# Revit family: RN 55048 Optipress-Therm-Raccordo
name_source: partatom
category: Rohrformteile
units: mm (PartAtom-declared; Revit-internal decimal feet)

## family parameters
Arbeitsebenenbasiert = Nein
Beim Laden mit Abzugskörper schneiden = Nein
Bemaßung runder Anschluss = Durchmesser verwenden
Gemeinsam genutzt = Nein
Immer vertikal = Ja
Teiletyp = Verbindung

## types (17) — shared parameters
1.010.00.2 Blattnummer der Richtlinie = 29
1.010.00.3 Ausgabedatum (Monat) der Richtlinie = 201308
1.010.00.4 Herstellername = R. Nussbaum AG
1.010.00.5 Revisionsdatum der Datei = 20190521
1.010.00.6 Webadresse des Herstellers = http://www.nussbaum.ch
1.100.00.4 Produktbezeichnung = Versorgung
1.110.00.2 Index = 1
1.110.00.4 Produktbezeichnung = Optipress-Therm
1.960/3L.00.8 Link (URL) = https://www.nussbaum.ch
29.700.00.4 Produktname = Optipress-Therm-Anschlussverschraubung, mit Pressmuffe
29.700.00.5 Produktkennung = 2
29.700.00.6 Querschnittsform = 1
29.700.00.7 Nennweitensystem = DN
29.700.00.8 Nenndrucksystem = PN
29.710.02.4 Nenndruck = 16
29.710.02.5 max. zul. Überdruck [hPa] = 1600
29.710.02.7 max. zul. Dauer-Betriebsdruck [hPa] = 1600
29.710.02.9 max. zul. Dauer-Betriebstemperatur [°C] = 95
Connector Visibility = Nein
EnclosingSpace Visibility = Nein
R. Nussbaum AG 55048.25 de Visibility = Nein

## per-type parameters (varying)
- DN=12x15: 1.800.00.3 TGA-Nummer=01900100000000000000000000000000000000000000000027000000000000000018; 1.800.00.4 Kommentarfeld=55048.22, Optipress-Therm-Anschlussverschraubung, mit Pressmuffe, DN=12x15, L=37; 1.810.00.3 Hersteller-Bestellnummer=55048.22; 1.810.00.4 DATANORM-Nummer=55048.22; 1.810.00.6 GTIN-Nummer=7612945815002; 29.710.02.10 Formstück-Gewicht [kg]=0.046; 29.710.02.3 Benennung=Optipress-Therm-Anschlussverschraubung, mit Pressmuffe, DN=12x15, L=37; CONNECTOR0_DIAMETER_dX_0r=12 mm  [stored 0.0393701 ft]; CONNECTOR0_dX_01=22 mm; CONNECTOR0_ref_dX=22 mm; CONNECTOR1_DIAMETER_dX_0r=15 mm  [stored 0.0492126 ft]; CONNECTOR1_dX_00=31 mm  [stored 0.101706 ft]; CONNECTOR1_dX_01=44 mm; CONNECTOR1_ref_dX=31 mm  [stored 0.101706 ft]; R. Nussbaum AG 55048.22 de Visibility=Ja; R. Nussbaum AG 55048.23 de Visibility=Nein; R. Nussbaum AG 55048.24 de Visibility=Nein; R. Nussbaum AG 55048.26 de Visibility=Nein; R. Nussbaum AG 55048.27 de Visibility=Nein; R. Nussbaum AG 55048.28 de Visibility=Nein; R. Nussbaum AG 55048.29 de Visibility=Nein; R. Nussbaum AG 55048.30 de Visibility=Nein; R. Nussbaum AG 55048.31 de Visibility=Nein; R. Nussbaum AG 55048.32 de Visibility=Nein; R. Nussbaum AG 55048.33 de Visibility=Nein; R. Nussbaum AG 55048.34 de Visibility=Nein; R. Nussbaum AG 55048.35 de Visibility=Nein; R. Nussbaum AG 55048.36 de Visibility=Nein; R. Nussbaum AG 55048.37 de Visibility=Nein; R. Nussbaum AG 55048.38 de Visibility=Nein; R. Nussbaum AG 55048.40 de Visibility=Nein
- DN=15: 1.800.00.3 TGA-Nummer=01900100000000000000000000000000000000000000000027000000000000000017; 1.800.00.4 Kommentarfeld=55048.40, Optipress-Therm-Anschlussverschraubung, mit Pressmuffe, DN=15, L=36; 1.810.00.3 Hersteller-Bestellnummer=55048.4; 1.810.00.4 DATANORM-Nummer=55048.40; 1.810.00.5 StLB-Nummer=256.112; 1.810.00.6 GTIN-Nummer=7612945709011; 29.710.02.10 Formstück-Gewicht [kg]=0.063; 29.710.02.3 Benennung=Optipress-Therm-Anschlussverschraubung, mit Pressmuffe, DN=15, L=36; CONNECTOR0_DIAMETER_dX_0r=15 mm  [stored 0.0492126 ft]; CONNECTOR0_dX_01=22 mm; CONNECTOR0_ref_dX=22 mm; CONNECTOR1_DIAMETER_dX_0r=20 mm; CONNECTOR1_dX_00=29 mm; CONNECTOR1_dX_01=44 mm; CONNECTOR1_ref_dX=29 mm; Hersteller=R. Nussbaum AG; Modell=55048.4; R. Nussbaum AG 55048.22 de Visibility=Nein; R. Nussbaum AG 55048.23 de Visibility=Nein; R. Nussbaum AG 55048.24 de Visibility=Nein; R. Nussbaum AG 55048.26 de Visibility=Nein; R. Nussbaum AG 55048.27 de Visibility=Nein; R. Nussbaum AG 55048.28 de Visibility=Nein; R. Nussbaum AG 55048.29 de Visibility=Nein; R. Nussbaum AG 55048.30 de Visibility=Nein; R. Nussbaum AG 55048.31 de Visibility=Nein; R. Nussbaum AG 55048.32 de Visibility=Nein; R. Nussbaum AG 55048.33 de Visibility=Nein; R. Nussbaum AG 55048.34 de Visibility=Nein; R. Nussbaum AG 55048.35 de Visibility=Nein; R. Nussbaum AG 55048.36 de Visibility=Nein; R. Nussbaum AG 55048.37 de Visibility=Nein; R. Nussbaum AG 55048.38 de Visibility=Nein; R. Nussbaum AG 55048.40 de Visibility=Ja; Typenkommentare=Optipress-Therm-Raccordo  DN=15
- DN=50: 1.800.00.3 TGA-Nummer=01900100000000000000000000000000000000000000000027000000000000000016; 1.800.00.4 Kommentarfeld=55048.30, Optipress-Therm-Anschlussverschraubung, mit Pressmuffe, DN=50, L=53; 1.810.00.3 Hersteller-Bestellnummer=55048.3; 1.810.00.4 DATANORM-Nummer=55048.30; 1.810.00.5 StLB-Nummer=256.168; 1.810.00.6 GTIN-Nummer=7612945663665; 29.710.02.10 Formstück-Gewicht [kg]=0.506; 29.710.02.3 Benennung=Optipress-Therm-Anschlussverschraubung, mit Pressmuffe, DN=50, L=53; CONNECTOR0_DIAMETER_dX_0r=50 mm; CONNECTOR0_dX_01=40 mm; CONNECTOR0_ref_dX=40 mm; CONNECTOR1_DIAMETER_dX_0r=50 mm; CONNECTOR1_dX_00=44 mm; CONNECTOR1_dX_01=68 mm; CONNECTOR1_ref_dX=44 mm; Hersteller=R. Nussbaum AG; Modell=55048.3; R. Nussbaum AG 55048.22 de Visibility=Nein; R. Nussbaum AG 55048.23 de Visibility=Nein; R. Nussbaum AG 55048.24 de Visibility=Nein; R. Nussbaum AG 55048.26 de Visibility=Nein; R. Nussbaum AG 55048.27 de Visibility=Nein; R. Nussbaum AG 55048.28 de Visibility=Nein; R. Nussbaum AG 55048.29 de Visibility=Nein; R. Nussbaum AG 55048.30 de Visibility=Ja; R. Nussbaum AG 55048.31 de Visibility=Nein; R. Nussbaum AG 55048.32 de Visibility=Nein; R. Nussbaum AG 55048.33 de Visibility=Nein; R. Nussbaum AG 55048.34 de Visibility=Nein; R. Nussbaum AG 55048.35 de Visibility=Nein; R. Nussbaum AG 55048.36 de Visibility=Nein; R. Nussbaum AG 55048.37 de Visibility=Nein; R. Nussbaum AG 55048.38 de Visibility=Nein; R. Nussbaum AG 55048.40 de Visibility=Nein; Typenkommentare=Optipress-Therm-Raccordo  DN=50
- DN=1: 1.800.00.3 TGA-Nummer=01900100000000000000000000000000000000000000000027000000000000000015; 1.800.00.4 Kommentarfeld=55048.38, Optipress-Therm-Anschlussverschraubung, mit Pressmuffe, DN=20, L=39; 1.810.00.3 Hersteller-Bestellnummer=55048.38; 1.810.00.4 DATANORM-Nummer=55048.38; 1.810.00.5 StLB-Nummer=256.124; 1.810.00.6 GTIN-Nummer=7612945692160; 29.710.02.10 Formstück-Gewicht [kg]=0.078; 29.710.02.3 Benennung=Optipress-Therm-Anschlussverschraubung, mit Pressmuffe, DN=20, L=39; CONNECTOR0_DIAMETER_dX_0r=20 mm; CONNECTOR0_dX_01=24 mm  [stored 0.0787402 ft]; CONNECTOR0_ref_dX=24 mm  [stored 0.0787402 ft]; CONNECTOR1_DIAMETER_dX_0r=20 mm; CONNECTOR1_dX_00=33 mm; CONNECTOR1_dX_01=48 mm; CONNECTOR1_ref_dX=33 mm; Hersteller=R. Nussbaum AG; Modell=55048.38; R. Nussbaum AG 55048.22 de Visibility=Nein; R. Nussbaum AG 55048.23 de Visibility=Nein; R. Nussbaum AG 55048.24 de Visibility=Nein; R. Nussbaum AG 55048.26 de Visibility=Nein; R. Nussbaum AG 55048.27 de Visibility=Nein; R. Nussbaum AG 55048.28 de Visibility=Nein; R. Nussbaum AG 55048.29 de Visibility=Nein; R. Nussbaum AG 55048.30 de Visibility=Nein; R. Nussbaum AG 55048.31 de Visibility=Nein; R. Nussbaum AG 55048.32 de Visibility=Nein; R. Nussbaum AG 55048.33 de Visibility=Nein; R. Nussbaum AG 55048.34 de Visibility=Nein; R. Nussbaum AG 55048.35 de Visibility=Nein; R. Nussbaum AG 55048.36 de Visibility=Nein; R. Nussbaum AG 55048.37 de Visibility=Nein; R. Nussbaum AG 55048.38 de Visibility=Ja; R. Nussbaum AG 55048.40 de Visibility=Nein; Typenkommentare=Optipress-Therm-Raccordo  DN=20
- DN=2: 1.800.00.3 TGA-Nummer=01900100000000000000000000000000000000000000000027000000000000000014; 1.800.00.4 Kommentarfeld=55048.37, Optipress-Therm-Anschlussverschraubung, mit Pressmuffe, DN=25, L=46; 1.810.00.3 Hersteller-Bestellnummer=55048.37; 1.810.00.4 DATANORM-Nummer=55048.37; 1.810.00.5 StLB-Nummer=256.135; 1.810.00.6 GTIN-Nummer=7612945688286; 29.710.02.10 Formstück-Gewicht [kg]=0.119; 29.710.02.3 Benennung=Optipress-Therm-Anschlussverschraubung, mit Pressmuffe, DN=25, L=46; CONNECTOR0_DIAMETER_dX_0r=25 mm  [stored 0.082021 ft]; CONNECTOR0_dX_01=24 mm  [stored 0.0787402 ft]; CONNECTOR0_ref_dX=24 mm  [stored 0.0787402 ft]; CONNECTOR1_DIAMETER_dX_0r=25 mm  [stored 0.082021 ft]; CONNECTOR1_dX_00=40 mm; CONNECTOR1_dX_01=57 mm; CONNECTOR1_ref_dX=40 mm; Hersteller=R. Nussbaum AG; Modell=55048.37; R. Nussbaum AG 55048.22 de Visibility=Nein; R. Nussbaum AG 55048.23 de Visibility=Nein; R. Nussbaum AG 55048.24 de Visibility=Nein; R. Nussbaum AG 55048.26 de Visibility=Nein; R. Nussbaum AG 55048.27 de Visibility=Nein; R. Nussbaum AG 55048.28 de Visibility=Nein; R. Nussbaum AG 55048.29 de Visibility=Nein; R. Nussbaum AG 55048.30 de Visibility=Nein; R. Nussbaum AG 55048.31 de Visibility=Nein; R. Nussbaum AG 55048.32 de Visibility=Nein; R. Nussbaum AG 55048.33 de Visibility=Nein; R. Nussbaum AG 55048.34 de Visibility=Nein; R. Nussbaum AG 55048.35 de Visibility=Nein; R. Nussbaum AG 55048.36 de Visibility=Nein; R. Nussbaum AG 55048.37 de Visibility=Ja; R. Nussbaum AG 55048.38 de Visibility=Nein; R. Nussbaum AG 55048.40 de Visibility=Nein; Typenkommentare=Optipress-Therm-Raccordo  DN=25
- DN=50x65: 1.800.00.3 TGA-Nummer=01900100000000000000000000000000000000000000000027000000000000000013; 1.800.00.4 Kommentarfeld=55048.36, Optipress-Therm-Anschlussverschraubung, mit Pressmuffe, DN=50x65, L=55; 1.810.00.3 Hersteller-Bestellnummer=55048.36; 1.810.00.4 DATANORM-Nummer=55048.36; 1.810.00.5 StLB-Nummer=256.168; 1.810.00.6 GTIN-Nummer=7612945685940; 29.710.02.10 Formstück-Gewicht [kg]=0.642; 29.710.02.3 Benennung=Optipress-Therm-Anschlussverschraubung, mit Pressmuffe, DN=50x65, L=55; CONNECTOR0_DIAMETER_dX_0r=50 mm; CONNECTOR0_dX_01=40 mm; CONNECTOR0_ref_dX=40 mm; CONNECTOR1_DIAMETER_dX_0r=65 mm; CONNECTOR1_dX_00=45 mm  [stored 0.147638 ft]; CONNECTOR1_dX_01=72 mm; CONNECTOR1_ref_dX=45 mm  [stored 0.147638 ft]; Hersteller=R. Nussbaum AG; Modell=55048.36; R. Nussbaum AG 55048.22 de Visibility=Nein; R. Nussbaum AG 55048.23 de Visibility=Nein; R. Nussbaum AG 55048.24 de Visibility=Nein; R. Nussbaum AG 55048.26 de Visibility=Nein; R. Nussbaum AG 55048.27 de Visibility=Nein; R. Nussbaum AG 55048.28 de Visibility=Nein; R. Nussbaum AG 55048.29 de Visibility=Nein; R. Nussbaum AG 55048.30 de Visibility=Nein; R. Nussbaum AG 55048.31 de Visibility=Nein; R. Nussbaum AG 55048.32 de Visibility=Nein; R. Nussbaum AG 55048.33 de Visibility=Nein; R. Nussbaum AG 55048.34 de Visibility=Nein; R. Nussbaum AG 55048.35 de Visibility=Nein; R. Nussbaum AG 55048.36 de Visibility=Ja; R. Nussbaum AG 55048.37 de Visibility=Nein; R. Nussbaum AG 55048.38 de Visibility=Nein; R. Nussbaum AG 55048.40 de Visibility=Nein; Typenkommentare=Optipress-Therm-Raccordo  DN=50x65
- DN=40x50: 1.800.00.3 TGA-Nummer=01900100000000000000000000000000000000000000000027000000000000000012; 1.800.00.4 Kommentarfeld=55048.35, Optipress-Therm-Anschlussverschraubung, mit Pressmuffe, DN=40x50, L=54; 1.810.00.3 Hersteller-Bestellnummer=55048.35; 1.810.00.4 DATANORM-Nummer=55048.35; 1.810.00.5 StLB-Nummer=256.157; 1.810.00.6 GTIN-Nummer=7612945685933; 29.710.02.10 Formstück-Gewicht [kg]=0.344; 29.710.02.3 Benennung=Optipress-Therm-Anschlussverschraubung, mit Pressmuffe, DN=40x50, L=54; CONNECTOR0_DIAMETER_dX_0r=40 mm; CONNECTOR0_dX_01=36 mm; CONNECTOR0_ref_dX=36 mm; CONNECTOR1_DIAMETER_dX_0r=50 mm; CONNECTOR1_dX_00=46 mm; CONNECTOR1_dX_01=70 mm; CONNECTOR1_ref_dX=46 mm; Hersteller=R. Nussbaum AG; Modell=55048.35; R. Nussbaum AG 55048.22 de Visibility=Nein; R. Nussbaum AG 55048.23 de Visibility=Nein; R. Nussbaum AG 55048.24 de Visibility=Nein; R. Nussbaum AG 55048.26 de Visibility=Nein; R. Nussbaum AG 55048.27 de Visibility=Nein; R. Nussbaum AG 55048.28 de Visibility=Nein; R. Nussbaum AG 55048.29 de Visibility=Nein; R. Nussbaum AG 55048.30 de Visibility=Nein; R. Nussbaum AG 55048.31 de Visibility=Nein; R. Nussbaum AG 55048.32 de Visibility=Nein; R. Nussbaum AG 55048.33 de Visibility=Nein; R. Nussbaum AG 55048.34 de Visibility=Nein; R. Nussbaum AG 55048.35 de Visibility=Ja; R. Nussbaum AG 55048.36 de Visibility=Nein; R. Nussbaum AG 55048.37 de Visibility=Nein; R. Nussbaum AG 55048.38 de Visibility=Nein; R. Nussbaum AG 55048.40 de Visibility=Nein; Typenkommentare=Optipress-Therm-Raccordo  DN=40x50
- DN=32x50: 1.800.00.3 TGA-Nummer=01900100000000000000000000000000000000000000000027000000000000000011; 1.800.00.4 Kommentarfeld=55048.34, Optipress-Therm-Anschlussverschraubung, mit Pressmuffe, DN=32x50, L=38; 1.810.00.3 Hersteller-Bestellnummer=55048.34; 1.810.00.4 DATANORM-Nummer=55048.34; 1.810.00.5 StLB-Nummer=256.146; 1.810.00.6 GTIN-Nummer=7612945685926; 29.710.02.10 Formstück-Gewicht [kg]=0.26; 29.710.02.3 Benennung=Optipress-Therm-Anschlussverschraubung, mit Pressmuffe, DN=32x50, L=38; CONNECTOR0_DIAMETER_dX_0r=32 mm  [stored 0.104987 ft]; CONNECTOR0_dX_01=26 mm; CONNECTOR0_ref_dX=26 mm; CONNECTOR1_DIAMETER_dX_0r=50 mm; CONNECTOR1_dX_00=27 mm; CONNECTOR1_dX_01=51 mm; CONNECTOR1_ref_dX=27 mm; Hersteller=R. Nussbaum AG; Modell=55048.34; R. Nussbaum AG 55048.22 de Visibility=Nein; R. Nussbaum AG 55048.23 de Visibility=Nein; R. Nussbaum AG 55048.24 de Visibility=Nein; R. Nussbaum AG 55048.26 de Visibility=Nein; R. Nussbaum AG 55048.27 de Visibility=Nein; R. Nussbaum AG 55048.28 de Visibility=Nein; R. Nussbaum AG 55048.29 de Visibility=Nein; R. Nussbaum AG 55048.30 de Visibility=Nein; R. Nussbaum AG 55048.31 de Visibility=Nein; R. Nussbaum AG 55048.32 de Visibility=Nein; R. Nussbaum AG 55048.33 de Visibility=Nein; R. Nussbaum AG 55048.34 de Visibility=Ja; R. Nussbaum AG 55048.35 de Visibility=Nein; R. Nussbaum AG 55048.36 de Visibility=Nein; R. Nussbaum AG 55048.37 de Visibility=Nein; R. Nussbaum AG 55048.38 de Visibility=Nein; R. Nussbaum AG 55048.40 de Visibility=Nein; Typenkommentare=Optipress-Therm-Raccordo  DN=32x50
- DN=25x32: 1.800.00.3 TGA-Nummer=01900100000000000000000000000000000000000000000027000000000000000010; 1.800.00.4 Kommentarfeld=55048.33, Optipress-Therm-Anschlussverschraubung, mit Pressmuffe, DN=25x32, L=36; 1.810.00.3 Hersteller-Bestellnummer=55048.33; 1.810.00.4 DATANORM-Nummer=55048.33; 1.810.00.5 StLB-Nummer=256.135; 1.810.00.6 GTIN-Nummer=7612945685919; 29.710.02.10 Formstück-Gewicht [kg]=0.174; 29.710.02.3 Benennung=Optipress-Therm-Anschlussverschraubung, mit Pressmuffe, DN=25x32, L=36; CONNECTOR0_DIAMETER_dX_0r=25 mm  [stored 0.082021 ft]; CONNECTOR0_dX_01=24 mm  [stored 0.0787402 ft]; CONNECTOR0_ref_dX=24 mm  [stored 0.0787402 ft]; CONNECTOR1_DIAMETER_dX_0r=40 mm; CONNECTOR1_dX_00=31 mm  [stored 0.101706 ft]; CONNECTOR1_dX_01=50 mm; CONNECTOR1_ref_dX=31 mm  [stored 0.101706 ft]; Hersteller=R. Nussbaum AG; Modell=55048.33; R. Nussbaum AG 55048.22 de Visibility=Nein; R. Nussbaum AG 55048.23 de Visibility=Nein; R. Nussbaum AG 55048.24 de Visibility=Nein; R. Nussbaum AG 55048.26 de Visibility=Nein; R. Nussbaum AG 55048.27 de Visibility=Nein; R. Nussbaum AG 55048.28 de Visibility=Nein; R. Nussbaum AG 55048.29 de Visibility=Nein; R. Nussbaum AG 55048.30 de Visibility=Nein; R. Nussbaum AG 55048.31 de Visibility=Nein; R. Nussbaum AG 55048.32 de Visibility=Nein; R. Nussbaum AG 55048.33 de Visibility=Ja; R. Nussbaum AG 55048.34 de Visibility=Nein; R. Nussbaum AG 55048.35 de Visibility=Nein; R. Nussbaum AG 55048.36 de Visibility=Nein; R. Nussbaum AG 55048.37 de Visibility=Nein; R. Nussbaum AG 55048.38 de Visibility=Nein; R. Nussbaum AG 55048.40 de Visibility=Nein; Typenkommentare=Optipress-Therm-Raccordo  DN=25x32
- DN=20x32: 1.800.00.3 TGA-Nummer=01900100000000000000000000000000000000000000000027000000000000000009; 1.800.00.4 Kommentarfeld=55048.32, Optipress-Therm-Anschlussverschraubung, mit Pressmuffe, DN=20x32, L=35; 1.810.00.3 Hersteller-Bestellnummer=55048.32; 1.810.00.4 DATANORM-Nummer=55048.32; 1.810.00.5 StLB-Nummer=256.124; 1.810.00.6 GTIN-Nummer=7612945685902; 29.710.02.10 Formstück-Gewicht [kg]=0.168; 29.710.02.3 Benennung=Optipress-Therm-Anschlussverschraubung, mit Pressmuffe, DN=20x32, L=35; CONNECTOR0_DIAMETER_dX_0r=20 mm; CONNECTOR0_dX_01=24 mm  [stored 0.0787402 ft]; CONNECTOR0_ref_dX=24 mm  [stored 0.0787402 ft]; CONNECTOR1_DIAMETER_dX_0r=40 mm; CONNECTOR1_dX_00=29 mm; CONNECTOR1_dX_01=48 mm; CONNECTOR1_ref_dX=29 mm; Hersteller=R. Nussbaum AG; Modell=55048.32; R. Nussbaum AG 55048.22 de Visibility=Nein; R. Nussbaum AG 55048.23 de Visibility=Nein; R. Nussbaum AG 55048.24 de Visibility=Nein; R. Nussbaum AG 55048.26 de Visibility=Nein; R. Nussbaum AG 55048.27 de Visibility=Nein; R. Nussbaum AG 55048.28 de Visibility=Nein; R. Nussbaum AG 55048.29 de Visibility=Nein; R. Nussbaum AG 55048.30 de Visibility=Nein; R. Nussbaum AG 55048.31 de Visibility=Nein; R. Nussbaum AG 55048.32 de Visibility=Ja; R. Nussbaum AG 55048.33 de Visibility=Nein; R. Nussbaum AG 55048.34 de Visibility=Nein; R. Nussbaum AG 55048.35 de Visibility=Nein; R. Nussbaum AG 55048.36 de Visibility=Nein; R. Nussbaum AG 55048.37 de Visibility=Nein; R. Nussbaum AG 55048.38 de Visibility=Nein; R. Nussbaum AG 55048.40 de Visibility=Nein; Typenkommentare=Optipress-Therm-Raccordo  DN=20x32
- DN=20x25: 1.800.00.3 TGA-Nummer=01900100000000000000000000000000000000000000000027000000000000000008; 1.800.00.4 Kommentarfeld=55048.31, Optipress-Therm-Anschlussverschraubung, mit Pressmuffe, DN=20x25, L=34; 1.810.00.3 Hersteller-Bestellnummer=55048.31; 1.810.00.4 DATANORM-Nummer=55048.31; 1.810.00.5 StLB-Nummer=256.124; 1.810.00.6 GTIN-Nummer=7612945685896; 29.710.02.10 Formstück-Gewicht [kg]=0.183; 29.710.02.3 Benennung=Optipress-Therm-Anschlussverschraubung, mit Pressmuffe, DN=20x25, L=34; CONNECTOR0_DIAMETER_dX_0r=20 mm; CONNECTOR0_dX_01=24 mm  [stored 0.0787402 ft]; CONNECTOR0_ref_dX=24 mm  [stored 0.0787402 ft]; CONNECTOR1_DIAMETER_dX_0r=32 mm  [stored 0.104987 ft]; CONNECTOR1_dX_00=28 mm; CONNECTOR1_dX_01=47 mm; CONNECTOR1_ref_dX=28 mm; Hersteller=R. Nussbaum AG; Modell=55048.31; R. Nussbaum AG 55048.22 de Visibility=Nein; R. Nussbaum AG 55048.23 de Visibility=Nein; R. Nussbaum AG 55048.24 de Visibility=Nein; R. Nussbaum AG 55048.26 de Visibility=Nein; R. Nussbaum AG 55048.27 de Visibility=Nein; R. Nussbaum AG 55048.28 de Visibility=Nein; R. Nussbaum AG 55048.29 de Visibility=Nein; R. Nussbaum AG 55048.30 de Visibility=Nein; R. Nussbaum AG 55048.31 de Visibility=Ja; R. Nussbaum AG 55048.32 de Visibility=Nein; R. Nussbaum AG 55048.33 de Visibility=Nein; R. Nussbaum AG 55048.34 de Visibility=Nein; R. Nussbaum AG 55048.35 de Visibility=Nein; R. Nussbaum AG 55048.36 de Visibility=Nein; R. Nussbaum AG 55048.37 de Visibility=Nein; R. Nussbaum AG 55048.38 de Visibility=Nein; R. Nussbaum AG 55048.40 de Visibility=Nein; Typenkommentare=Optipress-Therm-Raccordo  DN=20x25
- DN=40: 1.800.00.3 TGA-Nummer=01900100000000000000000000000000000000000000000027000000000000000007; 1.800.00.4 Kommentarfeld=55048.29, Optipress-Therm-Anschlussverschraubung, mit Pressmuffe, DN=40, L=46; 1.810.00.3 Hersteller-Bestellnummer=55048.29; 1.810.00.4 DATANORM-Nummer=55048.29; 1.810.00.5 StLB-Nummer=256.157; 1.810.00.6 GTIN-Nummer=7612945663658; 29.710.02.10 Formstück-Gewicht [kg]=0.281; 29.710.02.3 Benennung=Optipress-Therm-Anschlussverschraubung, mit Pressmuffe, DN=40, L=46; CONNECTOR0_DIAMETER_dX_0r=40 mm; CONNECTOR0_dX_01=36 mm; CONNECTOR0_ref_dX=36 mm; CONNECTOR1_DIAMETER_dX_0r=40 mm; CONNECTOR1_dX_00=40 mm; CONNECTOR1_dX_01=59 mm; CONNECTOR1_ref_dX=40 mm; Hersteller=R. Nussbaum AG; Modell=55048.29; R. Nussbaum AG 55048.22 de Visibility=Nein; R. Nussbaum AG 55048.23 de Visibility=Nein; R. Nussbaum AG 55048.24 de Visibility=Nein; R. Nussbaum AG 55048.26 de Visibility=Nein; R. Nussbaum AG 55048.27 de Visibility=Nein; R. Nussbaum AG 55048.28 de Visibility=Nein; R. Nussbaum AG 55048.29 de Visibility=Ja; R. Nussbaum AG 55048.30 de Visibility=Nein; R. Nussbaum AG 55048.31 de Visibility=Nein; R. Nussbaum AG 55048.32 de Visibility=Nein; R. Nussbaum AG 55048.33 de Visibility=Nein; R. Nussbaum AG 55048.34 de Visibility=Nein; R. Nussbaum AG 55048.35 de Visibility=Nein; R. Nussbaum AG 55048.36 de Visibility=Nein; R. Nussbaum AG 55048.37 de Visibility=Nein; R. Nussbaum AG 55048.38 de Visibility=Nein; R. Nussbaum AG 55048.40 de Visibility=Nein; Typenkommentare=Optipress-Therm-Raccordo  DN=40
- DN=32: 1.800.00.3 TGA-Nummer=01900100000000000000000000000000000000000000000027000000000000000006; 1.800.00.4 Kommentarfeld=55048.28, Optipress-Therm-Anschlussverschraubung, mit Pressmuffe, DN=32, L=37; 1.810.00.3 Hersteller-Bestellnummer=55048.28; 1.810.00.4 DATANORM-Nummer=55048.28; 1.810.00.5 StLB-Nummer=256.146; 1.810.00.6 GTIN-Nummer=7612945663641; 29.710.02.10 Formstück-Gewicht [kg]=0.188; 29.710.02.3 Benennung=Optipress-Therm-Anschlussverschraubung, mit Pressmuffe, DN=32, L=37; CONNECTOR0_DIAMETER_dX_0r=32 mm  [stored 0.104987 ft]; CONNECTOR0_dX_01=26 mm; CONNECTOR0_ref_dX=26 mm; CONNECTOR1_DIAMETER_dX_0r=40 mm; CONNECTOR1_dX_00=30 mm  [stored 0.0984252 ft]; CONNECTOR1_dX_01=49 mm; CONNECTOR1_ref_dX=30 mm  [stored 0.0984252 ft]; R. Nussbaum AG 55048.22 de Visibility=Nein; R. Nussbaum AG 55048.23 de Visibility=Nein; R. Nussbaum AG 55048.24 de Visibility=Nein; R. Nussbaum AG 55048.26 de Visibility=Nein; R. Nussbaum AG 55048.27 de Visibility=Nein; R. Nussbaum AG 55048.28 de Visibility=Ja; R. Nussbaum AG 55048.29 de Visibility=Nein; R. Nussbaum AG 55048.30 de Visibility=Nein; R. Nussbaum AG 55048.31 de Visibility=Nein; R. Nussbaum AG 55048.32 de Visibility=Nein; R. Nussbaum AG 55048.33 de Visibility=Nein; R. Nussbaum AG 55048.34 de Visibility=Nein; R. Nussbaum AG 55048.35 de Visibility=Nein; R. Nussbaum AG 55048.36 de Visibility=Nein; R. Nussbaum AG 55048.37 de Visibility=Nein; R. Nussbaum AG 55048.38 de Visibility=Nein; R. Nussbaum AG 55048.40 de Visibility=Nein
- DN=25: 1.800.00.3 TGA-Nummer=01900100000000000000000000000000000000000000000027000000000000000005; 1.800.00.4 Kommentarfeld=55048.27, Optipress-Therm-Anschlussverschraubung, mit Pressmuffe, DN=25, L=38; 1.810.00.3 Hersteller-Bestellnummer=55048.27; 1.810.00.4 DATANORM-Nummer=55048.27; 1.810.00.5 StLB-Nummer=256.135; 1.810.00.6 GTIN-Nummer=7612945663634; 29.710.02.10 Formstück-Gewicht [kg]=0.149; 29.710.02.3 Benennung=Optipress-Therm-Anschlussverschraubung, mit Pressmuffe, DN=25, L=38; CONNECTOR0_DIAMETER_dX_0r=25 mm  [stored 0.082021 ft]; CONNECTOR0_dX_01=24 mm  [stored 0.0787402 ft]; CONNECTOR0_ref_dX=24 mm  [stored 0.0787402 ft]; CONNECTOR1_DIAMETER_dX_0r=32 mm  [stored 0.104987 ft]; CONNECTOR1_dX_00=29 mm; CONNECTOR1_dX_01=48 mm; CONNECTOR1_ref_dX=29 mm; R. Nussbaum AG 55048.22 de Visibility=Nein; R. Nussbaum AG 55048.23 de Visibility=Nein; R. Nussbaum AG 55048.24 de Visibility=Nein; R. Nussbaum AG 55048.26 de Visibility=Nein; R. Nussbaum AG 55048.27 de Visibility=Ja; R. Nussbaum AG 55048.28 de Visibility=Nein; R. Nussbaum AG 55048.29 de Visibility=Nein; R. Nussbaum AG 55048.30 de Visibility=Nein; R. Nussbaum AG 55048.31 de Visibility=Nein; R. Nussbaum AG 55048.32 de Visibility=Nein; R. Nussbaum AG 55048.33 de Visibility=Nein; R. Nussbaum AG 55048.34 de Visibility=Nein; R. Nussbaum AG 55048.35 de Visibility=Nein; R. Nussbaum AG 55048.36 de Visibility=Nein; R. Nussbaum AG 55048.37 de Visibility=Nein; R. Nussbaum AG 55048.38 de Visibility=Nein; R. Nussbaum AG 55048.40 de Visibility=Nein
- DN=20: 1.800.00.3 TGA-Nummer=01900100000000000000000000000000000000000000000027000000000000000004; 1.800.00.4 Kommentarfeld=55048.26, Optipress-Therm-Anschlussverschraubung, mit Pressmuffe, DN=20, L=35; 1.810.00.3 Hersteller-Bestellnummer=55048.26; 1.810.00.4 DATANORM-Nummer=55048.26; 1.810.00.5 StLB-Nummer=256.124; 1.810.00.6 GTIN-Nummer=7612945663627; 29.710.02.10 Formstück-Gewicht [kg]=0.094; 29.710.02.3 Benennung=Optipress-Therm-Anschlussverschraubung, mit Pressmuffe, DN=20, L=35; CONNECTOR0_DIAMETER_dX_0r=20 mm; CONNECTOR0_dX_01=24 mm  [stored 0.0787402 ft]; CONNECTOR0_ref_dX=24 mm  [stored 0.0787402 ft]; CONNECTOR1_DIAMETER_dX_0r=25 mm  [stored 0.082021 ft]; CONNECTOR1_dX_00=27 mm; CONNECTOR1_dX_01=44 mm; CONNECTOR1_ref_dX=27 mm; R. Nussbaum AG 55048.22 de Visibility=Nein; R. Nussbaum AG 55048.23 de Visibility=Nein; R. Nussbaum AG 55048.24 de Visibility=Nein; R. Nussbaum AG 55048.26 de Visibility=Ja; R. Nussbaum AG 55048.27 de Visibility=Nein; R. Nussbaum AG 55048.28 de Visibility=Nein; R. Nussbaum AG 55048.29 de Visibility=Nein; R. Nussbaum AG 55048.30 de Visibility=Nein; R. Nussbaum AG 55048.31 de Visibility=Nein; R. Nussbaum AG 55048.32 de Visibility=Nein; R. Nussbaum AG 55048.33 de Visibility=Nein; R. Nussbaum AG 55048.34 de Visibility=Nein; R. Nussbaum AG 55048.35 de Visibility=Nein; R. Nussbaum AG 55048.36 de Visibility=Nein; R. Nussbaum AG 55048.37 de Visibility=Nein; R. Nussbaum AG 55048.38 de Visibility=Nein; R. Nussbaum AG 55048.40 de Visibility=Nein
- DN=15x20: 1.800.00.3 TGA-Nummer=01900100000000000000000000000000000000000000000027000000000000000002; 1.800.00.4 Kommentarfeld=55048.24, Optipress-Therm-Anschlussverschraubung, mit Pressmuffe, DN=15x20, L=31; 1.810.00.3 Hersteller-Bestellnummer=55048.24; 1.810.00.4 DATANORM-Nummer=55048.24; 1.810.00.5 StLB-Nummer=256.112; 1.810.00.6 GTIN-Nummer=7612945685872; 29.710.02.10 Formstück-Gewicht [kg]=0.076; 29.710.02.3 Benennung=Optipress-Therm-Anschlussverschraubung, mit Pressmuffe, DN=15x20, L=31; CONNECTOR0_DIAMETER_dX_0r=15 mm  [stored 0.0492126 ft]; CONNECTOR0_dX_01=22 mm; CONNECTOR0_ref_dX=22 mm; CONNECTOR1_DIAMETER_dX_0r=20 mm; CONNECTOR1_dX_00=24 mm  [stored 0.0787402 ft]; CONNECTOR1_dX_01=41 mm; CONNECTOR1_ref_dX=24 mm  [stored 0.0787402 ft]; R. Nussbaum AG 55048.22 de Visibility=Nein; R. Nussbaum AG 55048.23 de Visibility=Nein; R. Nussbaum AG 55048.24 de Visibility=Ja; R. Nussbaum AG 55048.26 de Visibility=Nein; R. Nussbaum AG 55048.27 de Visibility=Nein; R. Nussbaum AG 55048.28 de Visibility=Nein; R. Nussbaum AG 55048.29 de Visibility=Nein; R. Nussbaum AG 55048.30 de Visibility=Nein; R. Nussbaum AG 55048.31 de Visibility=Nein; R. Nussbaum AG 55048.32 de Visibility=Nein; R. Nussbaum AG 55048.33 de Visibility=Nein; R. Nussbaum AG 55048.34 de Visibility=Nein; R. Nussbaum AG 55048.35 de Visibility=Nein; R. Nussbaum AG 55048.36 de Visibility=Nein; R. Nussbaum AG 55048.37 de Visibility=Nein; R. Nussbaum AG 55048.38 de Visibility=Nein; R. Nussbaum AG 55048.40 de Visibility=Nein
- DN=12x20: 1.800.00.3 TGA-Nummer=01900100000000000000000000000000000000000000000027000000000000000001; 1.800.00.4 Kommentarfeld=55048.23, Optipress-Therm-Anschlussverschraubung, mit Pressmuffe, DN=12x20, L=32; 1.810.00.3 Hersteller-Bestellnummer=55048.23; 1.810.00.4 DATANORM-Nummer=55048.23; 1.810.00.5 StLB-Nummer=256.112; 1.810.00.6 GTIN-Nummer=7612945663603; 29.710.02.10 Formstück-Gewicht [kg]=0.064; 29.710.02.3 Benennung=Optipress-Therm-Anschlussverschraubung, mit Pressmuffe, DN=12x20, L=32; CONNECTOR0_DIAMETER_dX_0r=12 mm  [stored 0.0393701 ft]; CONNECTOR0_dX_01=22 mm; CONNECTOR0_ref_dX=22 mm; CONNECTOR1_DIAMETER_dX_0r=20 mm; CONNECTOR1_dX_00=28 mm; CONNECTOR1_dX_01=43 mm; CONNECTOR1_ref_dX=28 mm; R. Nussbaum AG 55048.22 de Visibility=Nein; R. Nussbaum AG 55048.23 de Visibility=Ja; R. Nussbaum AG 55048.24 de Visibility=Nein; R. Nussbaum AG 55048.26 de Visibility=Nein; R. Nussbaum AG 55048.27 de Visibility=Nein; R. Nussbaum AG 55048.28 de Visibility=Nein; R. Nussbaum AG 55048.29 de Visibility=Nein; R. Nussbaum AG 55048.30 de Visibility=Nein; R. Nussbaum AG 55048.31 de Visibility=Nein; R. Nussbaum AG 55048.32 de Visibility=Nein; R. Nussbaum AG 55048.33 de Visibility=Nein; R. Nussbaum AG 55048.34 de Visibility=Nein; R. Nussbaum AG 55048.35 de Visibility=Nein; R. Nussbaum AG 55048.36 de Visibility=Nein; R. Nussbaum AG 55048.37 de Visibility=Nein; R. Nussbaum AG 55048.38 de Visibility=Nein; R. Nussbaum AG 55048.40 de Visibility=Nein

note: [stored X ft] marks values corroborated as IEEE doubles in the binary element streams (Revit-internal decimal feet)

## geometry (parser evidence)
native form markers: Sweep x2
no freeform markers — native parametric forms only
